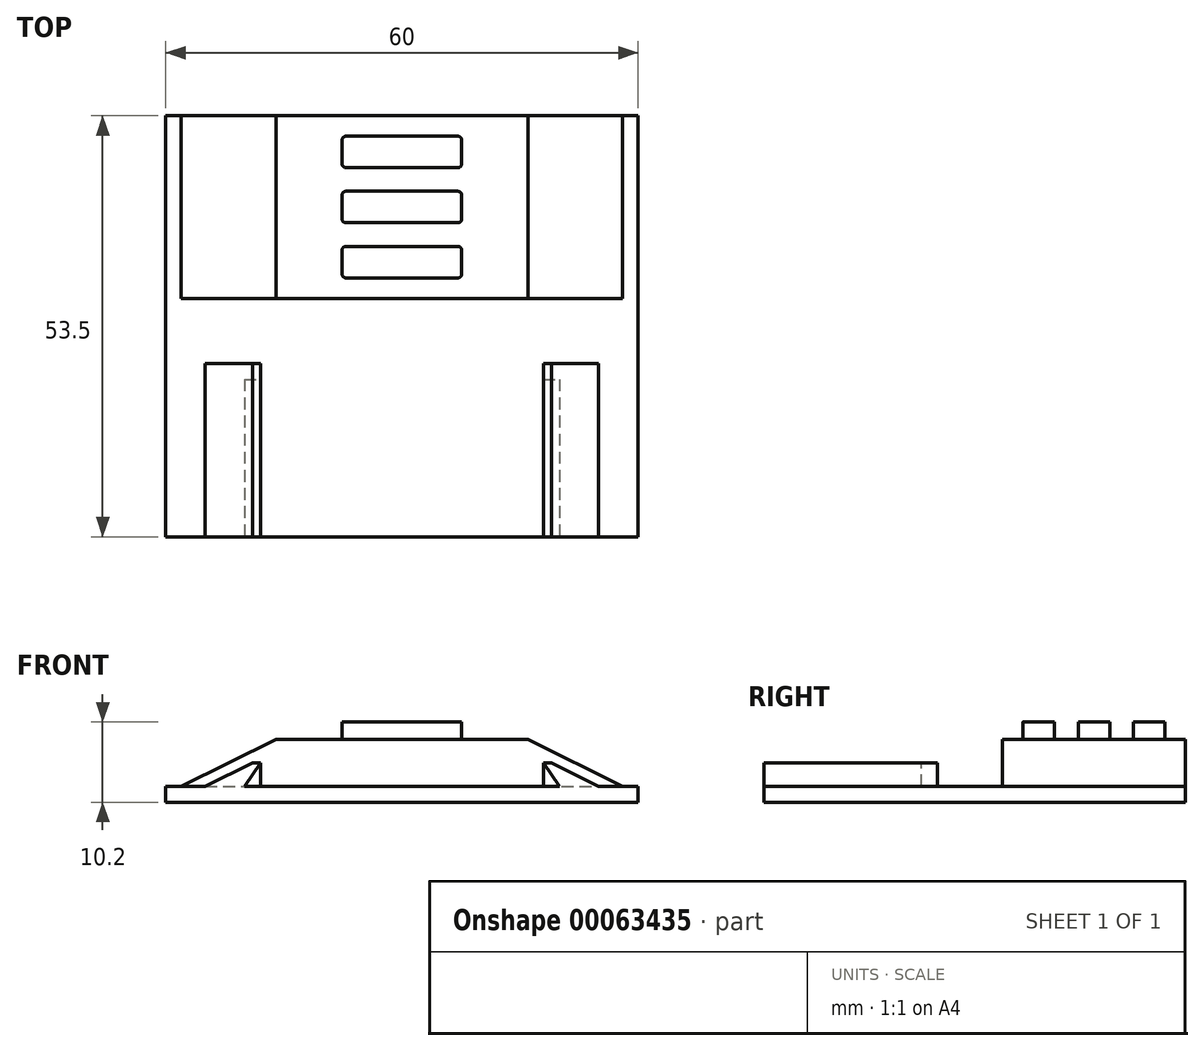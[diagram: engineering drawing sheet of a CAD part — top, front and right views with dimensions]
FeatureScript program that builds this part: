
annotation { "Feature Type Name" : "Feature", "Feature Type Description" : "" }
export const myFeature = defineFeature(function(context is Context, id is Id, definition is map)
    precondition{}
    {
        {
            var Q0;
            Q0=qCreatedBy(makeId("Top.planeOp"),FACE);
            var sketch = newSketch(context, id + "F0", { "sketchPlane" : qUnion([Q0])});
            skLineSegment(sketch, "E0.bottom", {"start": v(0, 0) * mm, "end": v(60, 0) * mm});
            skLineSegment(sketch, "E0.top", {"start": v(0, 53.5) * mm, "end": v(60, 53.5) * mm});
            skLineSegment(sketch, "E0.left", {"start": v(0, 0) * mm, "end": v(0, 53.5) * mm});
            skLineSegment(sketch, "E0.right", {"start": v(60, 0) * mm, "end": v(60, 53.5) * mm});
            skSolve(sketch);
        }
        {
            var Q0;
            Q0=makeQuery(id+"F0.imprint","IMPRINT",FACE,{"disambiguationData":[TD([[makeQuery(id+"F0.imprint","IMPRINT",EDGE,{"derivedFrom":sQuery(id+"F0.wireOp",EDGE,"E0.bottom")}),1.0]])]});
            extrude(context, id + "F1", {"entities" : qUnion([Q0]), "depth" : 2 * mm});
        }
        {
            var Q0;
            Q0=makeQuery(id+"F1.opExtrude","SWEPT_FACE",FACE,{"disambiguationData":[OSD([sQuery(id+"F0.wireOp",EDGE,"E0.top")])]});
            var sketch = newSketch(context, id + "F2", { "sketchPlane" : qUnion([Q0])});
            skLineSegment(sketch, "E1", {"start": v(-30, 0) * mm, "end": v(-30, 6.92) * mm, "construction": true});
            skLineSegment(sketch, "E2", {"start": v(-14, 8) * mm, "end": v(-1.95, 2) * mm});
            skLineSegment(sketch, "E3.MirrorCS", {"start": v(-46, 8) * mm, "end": v(-58.05, 2) * mm});
            skLineSegment(sketch, "E4", {"start": v(-1.95, 2) * mm, "end": v(-58.05, 2) * mm});
            skLineSegment(sketch, "E5", {"start": v(-46, 8) * mm, "end": v(-14, 8) * mm});
            skSolve(sketch);
        }
        {
            var Q0;
            Q0=makeQuery(id+"F2.imprint","IMPRINT",FACE,{"disambiguationData":[TD([[makeQuery(id+"F2.imprint","IMPRINT",EDGE,{"derivedFrom":sQuery(id+"F2.wireOp",EDGE,"E2")}),-1.0]])]});
            extrude(context, id + "F3", {"entities" : qUnion([Q0]), "operationType" : NewBodyOperationType.ADD, "oppositeDirection" : true, "depth" : 23.2 * mm});
        }
        {
            var Q0;
            Q0=makeQuery(id+"F3.opExtrude","SWEPT_FACE",FACE,{"disambiguationData":[OSD([sQuery(id+"F2.wireOp",EDGE,"E5")])]});
            var sketch = newSketch(context, id + "F4", { "sketchPlane" : qUnion([Q0])});
            skLineSegment(sketch, "E6", {"start": v(14, 41.9) * mm, "end": v(46, 41.9) * mm, "construction": true});
            skLineSegment(sketch, "E7", {"start": v(30, 53.5) * mm, "end": v(30, 30.3) * mm, "construction": true});
            skLineSegment(sketch, "E8.bottom", {"start": v(22.4, 43.9) * mm, "end": v(37.6, 43.9) * mm});
            skLineSegment(sketch, "E8.top", {"start": v(22.4, 39.9) * mm, "end": v(37.6, 39.9) * mm});
            skLineSegment(sketch, "E8.left", {"start": v(22.4, 43.9) * mm, "end": v(22.4, 39.9) * mm});
            skLineSegment(sketch, "E8.right", {"start": v(37.6, 43.9) * mm, "end": v(37.6, 39.9) * mm});
            skLineSegment(sketch, "E9.bottom", {"start": v(22.4, 46.9) * mm, "end": v(37.6, 46.9) * mm});
            skLineSegment(sketch, "E9.top", {"start": v(22.4, 50.9) * mm, "end": v(37.6, 50.9) * mm});
            skLineSegment(sketch, "E9.left", {"start": v(22.4, 46.9) * mm, "end": v(22.4, 50.9) * mm});
            skLineSegment(sketch, "E9.right", {"start": v(37.6, 46.9) * mm, "end": v(37.6, 50.9) * mm});
            skLineSegment(sketch, "E10.MirrorCS", {"start": v(22.4, 36.9) * mm, "end": v(22.4, 32.9) * mm});
            skLineSegment(sketch, "E11.MirrorCS", {"start": v(37.6, 36.9) * mm, "end": v(37.6, 32.9) * mm});
            skLineSegment(sketch, "E12.MirrorCS", {"start": v(22.4, 32.9) * mm, "end": v(37.6, 32.9) * mm});
            skLineSegment(sketch, "E13.MirrorCS", {"start": v(22.4, 36.9) * mm, "end": v(37.6, 36.9) * mm});
            skSolve(sketch);
        }
        {
            var Q0;
            Q0=makeQuery(id+"F4.imprint","IMPRINT",FACE,{"disambiguationData":[TD([[makeQuery(id+"F4.imprint","IMPRINT",EDGE,{"derivedFrom":sQuery(id+"F4.wireOp",EDGE,"E9.bottom")}),1.0]])]});
            var Q1;
            Q1=makeQuery(id+"F4.imprint","IMPRINT",FACE,{"disambiguationData":[TD([[makeQuery(id+"F4.imprint","IMPRINT",EDGE,{"derivedFrom":sQuery(id+"F4.wireOp",EDGE,"E8.bottom")}),-1.0]])]});
            var Q2;
            Q2=makeQuery(id+"F4.imprint","IMPRINT",FACE,{"disambiguationData":[TD([[makeQuery(id+"F4.imprint","IMPRINT",EDGE,{"derivedFrom":sQuery(id+"F4.wireOp",EDGE,"E10.MirrorCS")}),1.0]])]});
            extrude(context, id + "F5", {"entities" : qUnion([Q0, Q1, Q2]), "operationType" : NewBodyOperationType.ADD, "depth" : 2.2 * mm});
        }
        {
            var Q0;
            Q0=makeQuery(id+"F5.opExtrude","SWEPT_EDGE",EDGE,{"disambiguationData":[OSD([sQuery(id+"F4.wireOp",EDGE,"E9.bottom"),sQuery(id+"F4.wireOp",EDGE,"E9.left")])]});
            var Q1;
            Q1=makeQuery(id+"F5.opExtrude","SWEPT_EDGE",EDGE,{"disambiguationData":[OSD([sQuery(id+"F4.wireOp",EDGE,"E8.top"),sQuery(id+"F4.wireOp",EDGE,"E8.left")])]});
            var Q2;
            Q2=makeQuery(id+"F5.opExtrude","SWEPT_EDGE",EDGE,{"disambiguationData":[OSD([sQuery(id+"F4.wireOp",EDGE,"E10.MirrorCS"),sQuery(id+"F4.wireOp",EDGE,"E12.MirrorCS")])]});
            var Q3;
            Q3=makeQuery(id+"F5.opExtrude","SWEPT_EDGE",EDGE,{"disambiguationData":[OSD([sQuery(id+"F4.wireOp",EDGE,"E10.MirrorCS"),sQuery(id+"F4.wireOp",EDGE,"E13.MirrorCS")])]});
            var Q4;
            Q4=makeQuery(id+"F5.opExtrude","SWEPT_EDGE",EDGE,{"disambiguationData":[OSD([sQuery(id+"F4.wireOp",EDGE,"E8.bottom"),sQuery(id+"F4.wireOp",EDGE,"E8.left")])]});
            var Q5;
            Q5=makeQuery(id+"F5.opExtrude","SWEPT_EDGE",EDGE,{"disambiguationData":[OSD([sQuery(id+"F4.wireOp",EDGE,"E9.top"),sQuery(id+"F4.wireOp",EDGE,"E9.left")])]});
            var Q6;
            Q6=makeQuery(id+"F5.opExtrude","SWEPT_EDGE",EDGE,{"disambiguationData":[OSD([sQuery(id+"F4.wireOp",EDGE,"E11.MirrorCS"),sQuery(id+"F4.wireOp",EDGE,"E12.MirrorCS")])]});
            var Q7;
            Q7=makeQuery(id+"F5.opExtrude","SWEPT_EDGE",EDGE,{"disambiguationData":[OSD([sQuery(id+"F4.wireOp",EDGE,"E11.MirrorCS"),sQuery(id+"F4.wireOp",EDGE,"E13.MirrorCS")])]});
            var Q8;
            Q8=makeQuery(id+"F5.opExtrude","SWEPT_EDGE",EDGE,{"disambiguationData":[OSD([sQuery(id+"F4.wireOp",EDGE,"E8.top"),sQuery(id+"F4.wireOp",EDGE,"E8.right")])]});
            var Q9;
            Q9=makeQuery(id+"F5.opExtrude","SWEPT_EDGE",EDGE,{"disambiguationData":[OSD([sQuery(id+"F4.wireOp",EDGE,"E8.bottom"),sQuery(id+"F4.wireOp",EDGE,"E8.right")])]});
            var Q10;
            Q10=makeQuery(id+"F5.opExtrude","SWEPT_EDGE",EDGE,{"disambiguationData":[OSD([sQuery(id+"F4.wireOp",EDGE,"E9.bottom"),sQuery(id+"F4.wireOp",EDGE,"E9.right")])]});
            var Q11;
            Q11=makeQuery(id+"F5.opExtrude","SWEPT_EDGE",EDGE,{"disambiguationData":[OSD([sQuery(id+"F4.wireOp",EDGE,"E9.top"),sQuery(id+"F4.wireOp",EDGE,"E9.right")])]});
            fillet(context, id + "F6", {"entities" : qUnion([Q0, Q1, Q2, Q3, Q4, Q5, Q6, Q7, Q8, Q9, Q10, Q11]), "radius" : 0.5 * mm, "tangentPropagation" : true, "allowEdgeOverflow" : false});
        }
        {
            var Q0;
            Q0=makeQuery(id+"F1.opExtrude","SWEPT_FACE",FACE,{"disambiguationData":[OSD([sQuery(id+"F0.wireOp",EDGE,"E0.bottom")])]});
            var sketch = newSketch(context, id + "F7", { "sketchPlane" : qUnion([Q0])});
            skLineSegment(sketch, "E14", {"start": v(30, 0) * mm, "end": v(30, 14.53) * mm, "construction": true});
            skLineSegment(sketch, "E15", {"start": v(50, 2) * mm, "end": v(47.98, 5) * mm});
            skLineSegment(sketch, "E16", {"start": v(47.98, 5) * mm, "end": v(48.98, 5) * mm});
            skLineSegment(sketch, "E17", {"start": v(48.98, 5) * mm, "end": v(55, 2) * mm});
            skLineSegment(sketch, "E18.MirrorCS", {"start": v(12.02, 5) * mm, "end": v(11.02, 5) * mm});
            skLineSegment(sketch, "E19.MirrorCS", {"start": v(11.02, 5) * mm, "end": v(5, 2) * mm});
            skLineSegment(sketch, "E20.MirrorCS", {"start": v(10, 2) * mm, "end": v(12.02, 5) * mm});
            skSolve(sketch);
        }
        {
            var Q0;
            Q0=makeQuery(id+"F7.imprint","IMPRINT",FACE,{"disambiguationData":[TD([[makeQuery(id+"F7.imprint","IMPRINT",EDGE,{"derivedFrom":sQuery(id+"F7.wireOp",EDGE,"E18.MirrorCS")}),1.0]])]});
            var Q1;
            {var subQ0=sQuery(id+"F7.wireOp",EDGE,"E15");Q1=makeQuery(id+"F7.imprint","IMPRINT",FACE,{"disambiguationData":[TD([[makeQuery(id+"F7.imprint","IMPRINT",EDGE,{"derivedFrom":subQ0}),-1.0]])]});}
            extrude(context, id + "F8", {"entities" : qUnion([Q0, Q1]), "operationType" : NewBodyOperationType.ADD, "oppositeDirection" : true, "depth" : 20 * mm});
        }
        {
            var Q0;
            Q0=makeQuery(id+"F8.opExtrude","CAP_FACE",FACE,{"disambiguationData":[OSD([sQuery(id+"F0.wireOp",EDGE,"E0.bottom"),sQuery(id+"F7.wireOp",EDGE,"E18.MirrorCS"),sQuery(id+"F7.wireOp",EDGE,"E19.MirrorCS"),sQuery(id+"F7.wireOp",EDGE,"E20.MirrorCS")])],"isStart":false});
            var sketch = newSketch(context, id + "F9", { "sketchPlane" : qUnion([Q0])});
            skLineSegment(sketch, "E21", {"start": v(-5, 2) * mm, "end": v(-11.02, 5) * mm});
            skLineSegment(sketch, "E22", {"start": v(-11.02, 5) * mm, "end": v(-12.02, 5) * mm});
            skLineSegment(sketch, "E23", {"start": v(-12.02, 5) * mm, "end": v(-12.02, 2) * mm});
            skLineSegment(sketch, "E24", {"start": v(-12.02, 2) * mm, "end": v(-5, 2) * mm});
            skSolve(sketch);
        }
        {
            var Q0;
            Q0=makeQuery(id+"F8.opExtrude","CAP_FACE",FACE,{"disambiguationData":[OSD([sQuery(id+"F0.wireOp",EDGE,"E0.bottom"),sQuery(id+"F7.wireOp",EDGE,"E15"),sQuery(id+"F7.wireOp",EDGE,"E16"),sQuery(id+"F7.wireOp",EDGE,"E17")])],"isStart":false});
            var sketch = newSketch(context, id + "F10", { "sketchPlane" : qUnion([Q0])});
            skLineSegment(sketch, "E25", {"start": v(-55, 2) * mm, "end": v(-48.98, 5) * mm});
            skLineSegment(sketch, "E26", {"start": v(-48.98, 5) * mm, "end": v(-47.98, 5) * mm});
            skLineSegment(sketch, "E27", {"start": v(-47.98, 5) * mm, "end": v(-47.98, 2) * mm});
            skLineSegment(sketch, "E28", {"start": v(-47.98, 2) * mm, "end": v(-55, 2) * mm});
            skSolve(sketch);
        }
        {
            var Q0;
            {var subQ0=sQuery(id+"F9.wireOp",EDGE,"E21");Q0=makeQuery(id+"F9.imprint","IMPRINT",FACE,{"disambiguationData":[TD([[makeQuery(id+"F9.imprint","IMPRINT",EDGE,{"derivedFrom":subQ0}),-1.0]])]});}
            var Q1;
            {var subQ0=sQuery(id+"F9.wireOp",EDGE,"E23");Q1=makeQuery(id+"F9.imprint","IMPRINT",FACE,{"disambiguationData":[TD([[makeQuery(id+"F9.imprint","IMPRINT",EDGE,{"derivedFrom":subQ0}),1.0]])]});}
            var Q2;
            {var subQ0=sQuery(id+"F10.wireOp",EDGE,"E27");Q2=makeQuery(id+"F10.imprint","IMPRINT",FACE,{"disambiguationData":[TD([[makeQuery(id+"F10.imprint","IMPRINT",EDGE,{"derivedFrom":subQ0}),-1.0]])]});}
            var Q3;
            {var subQ0=sQuery(id+"F10.wireOp",EDGE,"E25");Q3=makeQuery(id+"F10.imprint","IMPRINT",FACE,{"disambiguationData":[TD([[makeQuery(id+"F10.imprint","IMPRINT",EDGE,{"derivedFrom":subQ0}),1.0]])]});}
            extrude(context, id + "F11", {"entities" : qUnion([Q0, Q1, Q2, Q3]), "operationType" : NewBodyOperationType.ADD, "depth" : 2 * mm});
        }
    });
